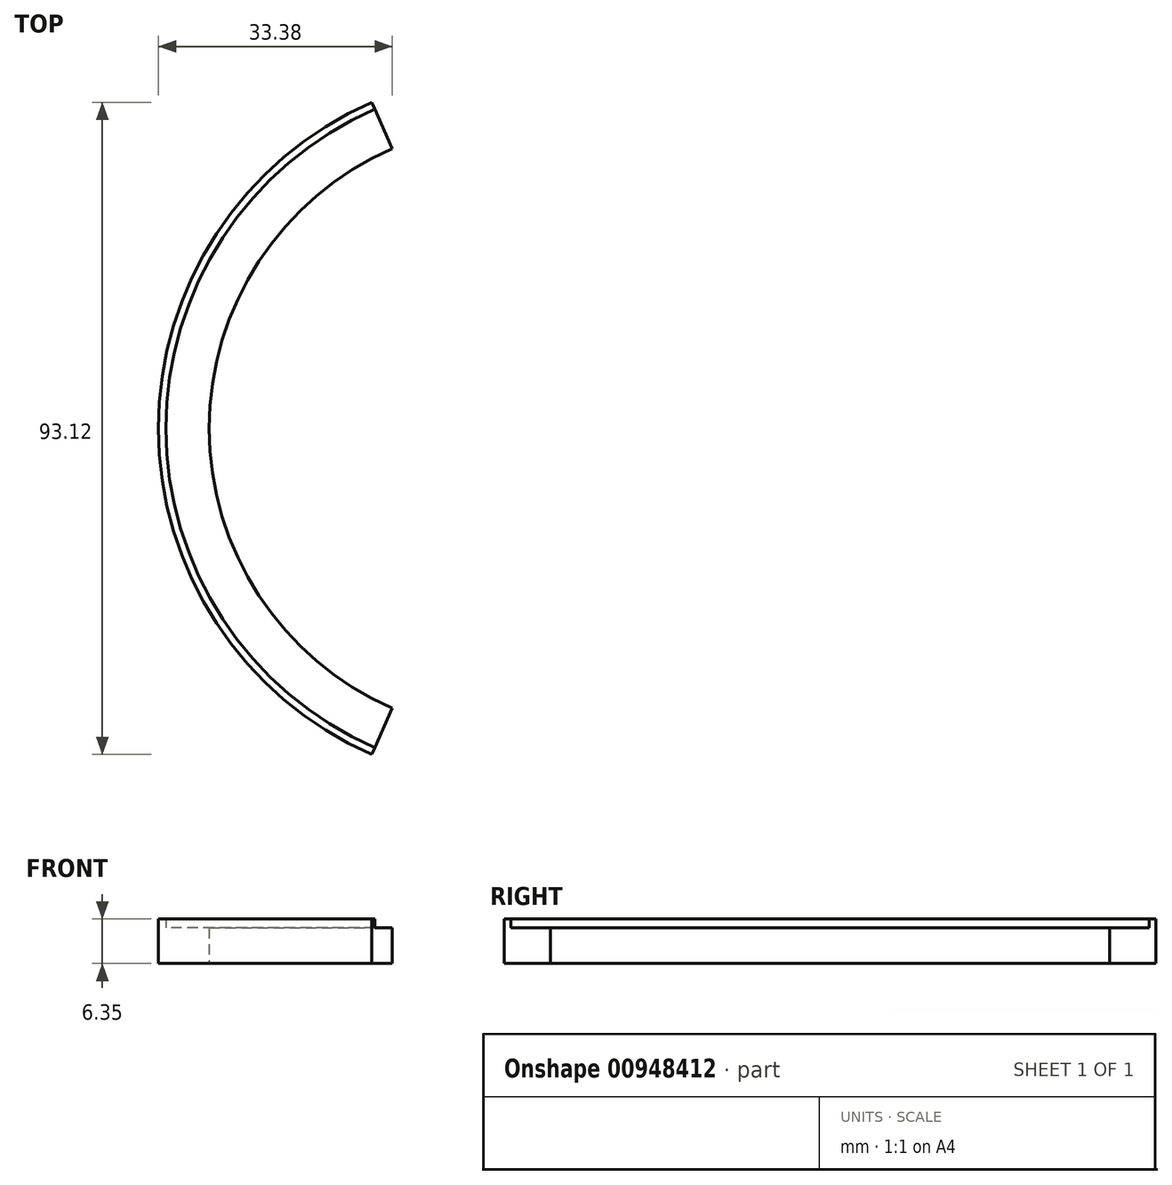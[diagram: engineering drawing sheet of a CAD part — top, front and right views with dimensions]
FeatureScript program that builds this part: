
annotation { "Feature Type Name" : "Feature", "Feature Type Description" : "" }
export const myFeature = defineFeature(function(context is Context, id is Id, definition is map)
    precondition{}
    {
        {
            var Q0;
            Q0=qCreatedBy(makeId("Top.planeOp"),FACE);
            var sketch = newSketch(context, id + "F0", { "sketchPlane" : qUnion([Q0])});
            skCircle(sketch, "E0", {"center": v(0, 0) * mm, "radius": 49.91 * mm, "construction": true});
            skCircle(sketch, "E1", {"center": v(0, 0) * mm, "radius": 43.56 * mm});
            skCircle(sketch, "E2", {"center": v(0, 0) * mm, "radius": 50.8 * mm});
            skSolve(sketch);
        }
        {
            var Q0;
            Q0 = qSketchRegion(id + "F0", true);
            extrude(context, id + "F1", {"entities" : qUnion([Q0]), "depth" : 5.08 * mm, "offsetDistance" : 25.4 * mm});
        }
        {
            var Q0;
            Q0=makeQuery(id+"F1.opExtrude","CAP_FACE",FACE,{"disambiguationData":[OSD([sQuery(id+"F0.wireOp",EDGE,"E1"),sQuery(id+"F0.wireOp",EDGE,"E2")])],"isStart":false});
            var sketch = newSketch(context, id + "F2", { "sketchPlane" : qUnion([Q0])});
            skCircle(sketch, "E3", {"center": v(0, 0) * mm, "radius": 50.8 * mm});
            skCircle(sketch, "E4", {"center": v(0, 0) * mm, "radius": 49.73 * mm});
            skSolve(sketch);
        }
        {
            var Q0;
            Q0 = qSketchRegion(id + "F2", true);
            extrude(context, id + "F3", {"entities" : qUnion([Q0]), "operationType" : NewBodyOperationType.ADD, "depth" : 1.27 * mm, "offsetDistance" : 25.4 * mm});
        }
        {
            var Q0;
            Q0=makeQuery(id+"F1.opExtrude","CAP_FACE",FACE,{"disambiguationData":[OSD([sQuery(id+"F0.wireOp",EDGE,"E1"),sQuery(id+"F0.wireOp",EDGE,"E2")])],"isStart":true});
            var sketch = newSketch(context, id + "F4", { "sketchPlane" : qUnion([Q0])});
            skLineSegment(sketch, "E5", {"start": v(0, 0) * mm, "end": v(0, 62.55) * mm, "construction": true});
            skCircle(sketch, "E6", {"center": v(0, 0) * mm, "radius": 53.34 * mm, "construction": true});
            skCircle(sketch, "E7", {"center": v(0, 0) * mm, "radius": 55.88 * mm, "construction": true});
            skLineSegment(sketch, "E8", {"start": v(2, 53.3) * mm, "end": v(-31.08, 54.54) * mm, "construction": true});
            skLineSegment(sketch, "E9", {"start": v(2, 53.3) * mm, "end": v(-26.14, 44.24) * mm, "construction": true});
            skLineSegment(sketch, "E10", {"start": v(0, 0) * mm, "end": v(-3.45, 92.16) * mm, "construction": true});
            skCircle(sketch, "E11", {"center": v(0, 0) * mm, "radius": 50.12 * mm, "construction": true});
            skArc(sketch, "E12.trimOffspring", {"start": v(2, 53.3) * mm, "mid": v(1.46, 54.62) * mm, "end": v(0.8, 55.87) * mm});
            skLineSegment(sketch, "E13", {"start": v(0.8, 55.87) * mm, "end": v(0, 55.87) * mm});
            skLineSegment(sketch, "E14", {"start": v(2, 53.3) * mm, "end": v(1.87, 49.86) * mm});
            skLineSegment(sketch, "E15", {"start": v(1.87, 49.86) * mm, "end": v(0, 49.86) * mm});
            skLineSegment(sketch, "E16.MirrorCS", {"start": v(-0.8, 55.87) * mm, "end": v(0, 55.87) * mm});
            skArc(sketch, "E17.MirrorCS", {"start": v(-2, 53.3) * mm, "mid": v(-1.46, 54.62) * mm, "end": v(-0.8, 55.87) * mm});
            skLineSegment(sketch, "E18.MirrorCS", {"start": v(-2, 53.3) * mm, "end": v(-1.87, 49.86) * mm});
            skLineSegment(sketch, "E19.MirrorCS", {"start": v(-1.87, 49.86) * mm, "end": v(0, 49.86) * mm});
            skSolve(sketch);
        }
        {
            var Q0;
            Q0 = qSketchRegion(id + "F4", true);
            extrude(context, id + "F5", {"entities" : qUnion([Q0]), "operationType" : NewBodyOperationType.ADD, "oppositeDirection" : true, "depth" : 6.35 * mm, "offsetDistance" : 25.4 * mm});
        }
        {
            var Q0;
            Q0=qCreatedBy(makeId("Front.planeOp"),FACE);
            var sketch = newSketch(context, id + "F6", { "sketchPlane" : qUnion([Q0])});
            skLineSegment(sketch, "E20", {"start": v(0, 0) * mm, "end": v(0, 10.44) * mm, "construction": true});
            skSolve(sketch);
        }
        {
            var Q0;
            {var subQ0=sQuery(id+"F4.wireOp",EDGE,"E19.MirrorCS");var subQ1=sQuery(id+"F4.wireOp",EDGE,"E18.MirrorCS");var subQ2=sQuery(id+"F4.wireOp",EDGE,"E17.MirrorCS");var subQ3=sQuery(id+"F4.wireOp",EDGE,"E16.MirrorCS");var subQ4=sQuery(id+"F4.wireOp",EDGE,"E15");var subQ5=sQuery(id+"F4.wireOp",EDGE,"E14");var subQ6=sQuery(id+"F4.wireOp",EDGE,"E13");var subQ7=sQuery(id+"F4.wireOp",EDGE,"E12.trimOffspring");Q0=makeQuery(id+"Fjfza61ILE3VkZQ_1.41.F5.boolean.opBoolean","MERGE",FACE,{"derivedFrom":[makeQuery(id+"Fjfza61ILE3VkZQ_1.40.F5.boolean.opBoolean","MERGE",FACE,{"derivedFrom":[makeQuery(id+"Fjfza61ILE3VkZQ_1.39.F5.boolean.opBoolean","MERGE",FACE,{"derivedFrom":[makeQuery(id+"Fjfza61ILE3VkZQ_1.38.F5.boolean.opBoolean","MERGE",FACE,{"derivedFrom":[makeQuery(id+"Fjfza61ILE3VkZQ_1.37.F5.boolean.opBoolean","MERGE",FACE,{"derivedFrom":[makeQuery(id+"Fjfza61ILE3VkZQ_1.36.F5.boolean.opBoolean","MERGE",FACE,{"derivedFrom":[makeQuery(id+"Fjfza61ILE3VkZQ_1.35.F5.boolean.opBoolean","MERGE",FACE,{"derivedFrom":[makeQuery(id+"Fjfza61ILE3VkZQ_1.34.F5.boolean.opBoolean","MERGE",FACE,{"derivedFrom":[makeQuery(id+"Fjfza61ILE3VkZQ_1.33.F5.boolean.opBoolean","MERGE",FACE,{"derivedFrom":[makeQuery(id+"Fjfza61ILE3VkZQ_1.32.F5.boolean.opBoolean","MERGE",FACE,{"derivedFrom":[makeQuery(id+"Fjfza61ILE3VkZQ_1.31.F5.boolean.opBoolean","MERGE",FACE,{"derivedFrom":[makeQuery(id+"Fjfza61ILE3VkZQ_1.30.F5.boolean.opBoolean","MERGE",FACE,{"derivedFrom":[makeQuery(id+"Fjfza61ILE3VkZQ_1.29.F5.boolean.opBoolean","MERGE",FACE,{"derivedFrom":[makeQuery(id+"Fjfza61ILE3VkZQ_1.28.F5.boolean.opBoolean","MERGE",FACE,{"derivedFrom":[makeQuery(id+"Fjfza61ILE3VkZQ_1.27.F5.boolean.opBoolean","MERGE",FACE,{"derivedFrom":[makeQuery(id+"Fjfza61ILE3VkZQ_1.26.F5.boolean.opBoolean","MERGE",FACE,{"derivedFrom":[makeQuery(id+"Fjfza61ILE3VkZQ_1.25.F5.boolean.opBoolean","MERGE",FACE,{"derivedFrom":[makeQuery(id+"Fjfza61ILE3VkZQ_1.24.F5.boolean.opBoolean","MERGE",FACE,{"derivedFrom":[makeQuery(id+"Fjfza61ILE3VkZQ_1.23.F5.boolean.opBoolean","MERGE",FACE,{"derivedFrom":[makeQuery(id+"Fjfza61ILE3VkZQ_1.22.F5.boolean.opBoolean","MERGE",FACE,{"derivedFrom":[makeQuery(id+"Fjfza61ILE3VkZQ_1.21.F5.boolean.opBoolean","MERGE",FACE,{"derivedFrom":[makeQuery(id+"Fjfza61ILE3VkZQ_1.20.F5.boolean.opBoolean","MERGE",FACE,{"derivedFrom":[makeQuery(id+"Fjfza61ILE3VkZQ_1.19.F5.boolean.opBoolean","MERGE",FACE,{"derivedFrom":[makeQuery(id+"Fjfza61ILE3VkZQ_1.18.F5.boolean.opBoolean","MERGE",FACE,{"derivedFrom":[makeQuery(id+"Fjfza61ILE3VkZQ_1.17.F5.boolean.opBoolean","MERGE",FACE,{"derivedFrom":[makeQuery(id+"Fjfza61ILE3VkZQ_1.16.F5.boolean.opBoolean","MERGE",FACE,{"derivedFrom":[makeQuery(id+"Fjfza61ILE3VkZQ_1.15.F5.boolean.opBoolean","MERGE",FACE,{"derivedFrom":[makeQuery(id+"Fjfza61ILE3VkZQ_1.14.F5.boolean.opBoolean","MERGE",FACE,{"derivedFrom":[makeQuery(id+"Fjfza61ILE3VkZQ_1.13.F5.boolean.opBoolean","MERGE",FACE,{"derivedFrom":[makeQuery(id+"Fjfza61ILE3VkZQ_1.12.F5.boolean.opBoolean","MERGE",FACE,{"derivedFrom":[makeQuery(id+"Fjfza61ILE3VkZQ_1.11.F5.boolean.opBoolean","MERGE",FACE,{"derivedFrom":[makeQuery(id+"Fjfza61ILE3VkZQ_1.10.F5.boolean.opBoolean","MERGE",FACE,{"derivedFrom":[makeQuery(id+"Fjfza61ILE3VkZQ_1.9.F5.boolean.opBoolean","MERGE",FACE,{"derivedFrom":[makeQuery(id+"Fjfza61ILE3VkZQ_1.8.F5.boolean.opBoolean","MERGE",FACE,{"derivedFrom":[makeQuery(id+"Fjfza61ILE3VkZQ_1.7.F5.boolean.opBoolean","MERGE",FACE,{"derivedFrom":[makeQuery(id+"Fjfza61ILE3VkZQ_1.6.F5.boolean.opBoolean","MERGE",FACE,{"derivedFrom":[makeQuery(id+"Fjfza61ILE3VkZQ_1.5.F5.boolean.opBoolean","MERGE",FACE,{"derivedFrom":[makeQuery(id+"Fjfza61ILE3VkZQ_1.4.F5.boolean.opBoolean","MERGE",FACE,{"derivedFrom":[makeQuery(id+"Fjfza61ILE3VkZQ_1.3.F5.boolean.opBoolean","MERGE",FACE,{"derivedFrom":[makeQuery(id+"Fjfza61ILE3VkZQ_1.2.F5.boolean.opBoolean","MERGE",FACE,{"derivedFrom":[makeQuery(id+"Fjfza61ILE3VkZQ_1.1.F5.boolean.opBoolean","MERGE",FACE,{"derivedFrom":[makeQuery(id+"F5.boolean.opBoolean","MERGE",FACE,{"derivedFrom":[makeQuery(id+"F1.opExtrude","CAP_FACE",FACE,{"disambiguationData":[OSD([sQuery(id+"F0.wireOp",EDGE,"E1"),sQuery(id+"F0.wireOp",EDGE,"E2")])],"isStart":true}),makeQuery(id+"F5.opExtrude","CAP_FACE",FACE,{"disambiguationData":[OSD([subQ7,subQ6,subQ5,subQ4,subQ3,subQ2,subQ1,subQ0])],"isStart":true})]}),makeQuery(id+"Fjfza61ILE3VkZQ_1.1.F5.opExtrude","CAP_FACE",FACE,{"disambiguationData":[OSD([subQ7,subQ6,subQ5,subQ4,subQ3,subQ2,subQ1,subQ0])],"isStart":true})]}),makeQuery(id+"Fjfza61ILE3VkZQ_1.2.F5.opExtrude","CAP_FACE",FACE,{"disambiguationData":[OSD([subQ7,subQ6,subQ5,subQ4,subQ3,subQ2,subQ1,subQ0])],"isStart":true})]}),makeQuery(id+"Fjfza61ILE3VkZQ_1.3.F5.opExtrude","CAP_FACE",FACE,{"disambiguationData":[OSD([subQ7,subQ6,subQ5,subQ4,subQ3,subQ2,subQ1,subQ0])],"isStart":true})]}),makeQuery(id+"Fjfza61ILE3VkZQ_1.4.F5.opExtrude","CAP_FACE",FACE,{"disambiguationData":[OSD([subQ7,subQ6,subQ5,subQ4,subQ3,subQ2,subQ1,subQ0])],"isStart":true})]}),makeQuery(id+"Fjfza61ILE3VkZQ_1.5.F5.opExtrude","CAP_FACE",FACE,{"disambiguationData":[OSD([subQ7,subQ6,subQ5,subQ4,subQ3,subQ2,subQ1,subQ0])],"isStart":true})]}),makeQuery(id+"Fjfza61ILE3VkZQ_1.6.F5.opExtrude","CAP_FACE",FACE,{"disambiguationData":[OSD([subQ7,subQ6,subQ5,subQ4,subQ3,subQ2,subQ1,subQ0])],"isStart":true})]}),makeQuery(id+"Fjfza61ILE3VkZQ_1.7.F5.opExtrude","CAP_FACE",FACE,{"disambiguationData":[OSD([subQ7,subQ6,subQ5,subQ4,subQ3,subQ2,subQ1,subQ0])],"isStart":true})]}),makeQuery(id+"Fjfza61ILE3VkZQ_1.8.F5.opExtrude","CAP_FACE",FACE,{"disambiguationData":[OSD([subQ7,subQ6,subQ5,subQ4,subQ3,subQ2,subQ1,subQ0])],"isStart":true})]}),makeQuery(id+"Fjfza61ILE3VkZQ_1.9.F5.opExtrude","CAP_FACE",FACE,{"disambiguationData":[OSD([subQ7,subQ6,subQ5,subQ4,subQ3,subQ2,subQ1,subQ0])],"isStart":true})]}),makeQuery(id+"Fjfza61ILE3VkZQ_1.10.F5.opExtrude","CAP_FACE",FACE,{"disambiguationData":[OSD([subQ7,subQ6,subQ5,subQ4,subQ3,subQ2,subQ1,subQ0])],"isStart":true})]}),makeQuery(id+"Fjfza61ILE3VkZQ_1.11.F5.opExtrude","CAP_FACE",FACE,{"disambiguationData":[OSD([subQ7,subQ6,subQ5,subQ4,subQ3,subQ2,subQ1,subQ0])],"isStart":true})]}),makeQuery(id+"Fjfza61ILE3VkZQ_1.12.F5.opExtrude","CAP_FACE",FACE,{"disambiguationData":[OSD([subQ7,subQ6,subQ5,subQ4,subQ3,subQ2,subQ1,subQ0])],"isStart":true})]}),makeQuery(id+"Fjfza61ILE3VkZQ_1.13.F5.opExtrude","CAP_FACE",FACE,{"disambiguationData":[OSD([subQ7,subQ6,subQ5,subQ4,subQ3,subQ2,subQ1,subQ0])],"isStart":true})]}),makeQuery(id+"Fjfza61ILE3VkZQ_1.14.F5.opExtrude","CAP_FACE",FACE,{"disambiguationData":[OSD([subQ7,subQ6,subQ5,subQ4,subQ3,subQ2,subQ1,subQ0])],"isStart":true})]}),makeQuery(id+"Fjfza61ILE3VkZQ_1.15.F5.opExtrude","CAP_FACE",FACE,{"disambiguationData":[OSD([subQ7,subQ6,subQ5,subQ4,subQ3,subQ2,subQ1,subQ0])],"isStart":true})]}),makeQuery(id+"Fjfza61ILE3VkZQ_1.16.F5.opExtrude","CAP_FACE",FACE,{"disambiguationData":[OSD([subQ7,subQ6,subQ5,subQ4,subQ3,subQ2,subQ1,subQ0])],"isStart":true})]}),makeQuery(id+"Fjfza61ILE3VkZQ_1.17.F5.opExtrude","CAP_FACE",FACE,{"disambiguationData":[OSD([subQ7,subQ6,subQ5,subQ4,subQ3,subQ2,subQ1,subQ0])],"isStart":true})]}),makeQuery(id+"Fjfza61ILE3VkZQ_1.18.F5.opExtrude","CAP_FACE",FACE,{"disambiguationData":[OSD([subQ7,subQ6,subQ5,subQ4,subQ3,subQ2,subQ1,subQ0])],"isStart":true})]}),makeQuery(id+"Fjfza61ILE3VkZQ_1.19.F5.opExtrude","CAP_FACE",FACE,{"disambiguationData":[OSD([subQ7,subQ6,subQ5,subQ4,subQ3,subQ2,subQ1,subQ0])],"isStart":true})]}),makeQuery(id+"Fjfza61ILE3VkZQ_1.20.F5.opExtrude","CAP_FACE",FACE,{"disambiguationData":[OSD([subQ7,subQ6,subQ5,subQ4,subQ3,subQ2,subQ1,subQ0])],"isStart":true})]}),makeQuery(id+"Fjfza61ILE3VkZQ_1.21.F5.opExtrude","CAP_FACE",FACE,{"disambiguationData":[OSD([subQ7,subQ6,subQ5,subQ4,subQ3,subQ2,subQ1,subQ0])],"isStart":true})]}),makeQuery(id+"Fjfza61ILE3VkZQ_1.22.F5.opExtrude","CAP_FACE",FACE,{"disambiguationData":[OSD([subQ7,subQ6,subQ5,subQ4,subQ3,subQ2,subQ1,subQ0])],"isStart":true})]}),makeQuery(id+"Fjfza61ILE3VkZQ_1.23.F5.opExtrude","CAP_FACE",FACE,{"disambiguationData":[OSD([subQ7,subQ6,subQ5,subQ4,subQ3,subQ2,subQ1,subQ0])],"isStart":true})]}),makeQuery(id+"Fjfza61ILE3VkZQ_1.24.F5.opExtrude","CAP_FACE",FACE,{"disambiguationData":[OSD([subQ7,subQ6,subQ5,subQ4,subQ3,subQ2,subQ1,subQ0])],"isStart":true})]}),makeQuery(id+"Fjfza61ILE3VkZQ_1.25.F5.opExtrude","CAP_FACE",FACE,{"disambiguationData":[OSD([subQ7,subQ6,subQ5,subQ4,subQ3,subQ2,subQ1,subQ0])],"isStart":true})]}),makeQuery(id+"Fjfza61ILE3VkZQ_1.26.F5.opExtrude","CAP_FACE",FACE,{"disambiguationData":[OSD([subQ7,subQ6,subQ5,subQ4,subQ3,subQ2,subQ1,subQ0])],"isStart":true})]}),makeQuery(id+"Fjfza61ILE3VkZQ_1.27.F5.opExtrude","CAP_FACE",FACE,{"disambiguationData":[OSD([subQ7,subQ6,subQ5,subQ4,subQ3,subQ2,subQ1,subQ0])],"isStart":true})]}),makeQuery(id+"Fjfza61ILE3VkZQ_1.28.F5.opExtrude","CAP_FACE",FACE,{"disambiguationData":[OSD([subQ7,subQ6,subQ5,subQ4,subQ3,subQ2,subQ1,subQ0])],"isStart":true})]}),makeQuery(id+"Fjfza61ILE3VkZQ_1.29.F5.opExtrude","CAP_FACE",FACE,{"disambiguationData":[OSD([subQ7,subQ6,subQ5,subQ4,subQ3,subQ2,subQ1,subQ0])],"isStart":true})]}),makeQuery(id+"Fjfza61ILE3VkZQ_1.30.F5.opExtrude","CAP_FACE",FACE,{"disambiguationData":[OSD([subQ7,subQ6,subQ5,subQ4,subQ3,subQ2,subQ1,subQ0])],"isStart":true})]}),makeQuery(id+"Fjfza61ILE3VkZQ_1.31.F5.opExtrude","CAP_FACE",FACE,{"disambiguationData":[OSD([subQ7,subQ6,subQ5,subQ4,subQ3,subQ2,subQ1,subQ0])],"isStart":true})]}),makeQuery(id+"Fjfza61ILE3VkZQ_1.32.F5.opExtrude","CAP_FACE",FACE,{"disambiguationData":[OSD([subQ7,subQ6,subQ5,subQ4,subQ3,subQ2,subQ1,subQ0])],"isStart":true})]}),makeQuery(id+"Fjfza61ILE3VkZQ_1.33.F5.opExtrude","CAP_FACE",FACE,{"disambiguationData":[OSD([subQ7,subQ6,subQ5,subQ4,subQ3,subQ2,subQ1,subQ0])],"isStart":true})]}),makeQuery(id+"Fjfza61ILE3VkZQ_1.34.F5.opExtrude","CAP_FACE",FACE,{"disambiguationData":[OSD([subQ7,subQ6,subQ5,subQ4,subQ3,subQ2,subQ1,subQ0])],"isStart":true})]}),makeQuery(id+"Fjfza61ILE3VkZQ_1.35.F5.opExtrude","CAP_FACE",FACE,{"disambiguationData":[OSD([subQ7,subQ6,subQ5,subQ4,subQ3,subQ2,subQ1,subQ0])],"isStart":true})]}),makeQuery(id+"Fjfza61ILE3VkZQ_1.36.F5.opExtrude","CAP_FACE",FACE,{"disambiguationData":[OSD([subQ7,subQ6,subQ5,subQ4,subQ3,subQ2,subQ1,subQ0])],"isStart":true})]}),makeQuery(id+"Fjfza61ILE3VkZQ_1.37.F5.opExtrude","CAP_FACE",FACE,{"disambiguationData":[OSD([subQ7,subQ6,subQ5,subQ4,subQ3,subQ2,subQ1,subQ0])],"isStart":true})]}),makeQuery(id+"Fjfza61ILE3VkZQ_1.38.F5.opExtrude","CAP_FACE",FACE,{"disambiguationData":[OSD([subQ7,subQ6,subQ5,subQ4,subQ3,subQ2,subQ1,subQ0])],"isStart":true})]}),makeQuery(id+"Fjfza61ILE3VkZQ_1.39.F5.opExtrude","CAP_FACE",FACE,{"disambiguationData":[OSD([subQ7,subQ6,subQ5,subQ4,subQ3,subQ2,subQ1,subQ0])],"isStart":true})]}),makeQuery(id+"Fjfza61ILE3VkZQ_1.40.F5.opExtrude","CAP_FACE",FACE,{"disambiguationData":[OSD([subQ7,subQ6,subQ5,subQ4,subQ3,subQ2,subQ1,subQ0])],"isStart":true})]}),makeQuery(id+"Fjfza61ILE3VkZQ_1.41.F5.opExtrude","CAP_FACE",FACE,{"disambiguationData":[OSD([subQ7,subQ6,subQ5,subQ4,subQ3,subQ2,subQ1,subQ0])],"isStart":true})]});}
            var sketch = newSketch(context, id + "F7", { "sketchPlane" : qUnion([Q0])});
            skArc(sketch, "E21", {"start": v(-25.88, -59.32) * mm, "mid": v(64.72, 0) * mm, "end": v(-25.88, 59.32) * mm});
            skLineSegment(sketch, "E22", {"start": v(0, 0) * mm, "end": v(-20.31, 46.56) * mm});
            skLineSegment(sketch, "E23", {"start": v(-20.31, 46.56) * mm, "end": v(-25.88, 59.32) * mm});
            skLineSegment(sketch, "E24", {"start": v(0, 0) * mm, "end": v(-86.7, 0) * mm, "construction": true});
            skLineSegment(sketch, "E25.MirrorCS", {"start": v(0, 0) * mm, "end": v(-20.31, -46.56) * mm});
            skLineSegment(sketch, "E26.MirrorCS", {"start": v(-20.31, -46.56) * mm, "end": v(-25.88, -59.32) * mm});
            skSolve(sketch);
        }
        {
            var Q0;
            Q0 = qSketchRegion(id + "F7", true);
            extrude(context, id + "F8", {"entities" : qUnion([Q0]), "operationType" : NewBodyOperationType.REMOVE, "oppositeDirection" : true, "depth" : 25.4 * mm, "offsetDistance" : 25.4 * mm});
        }
    });
